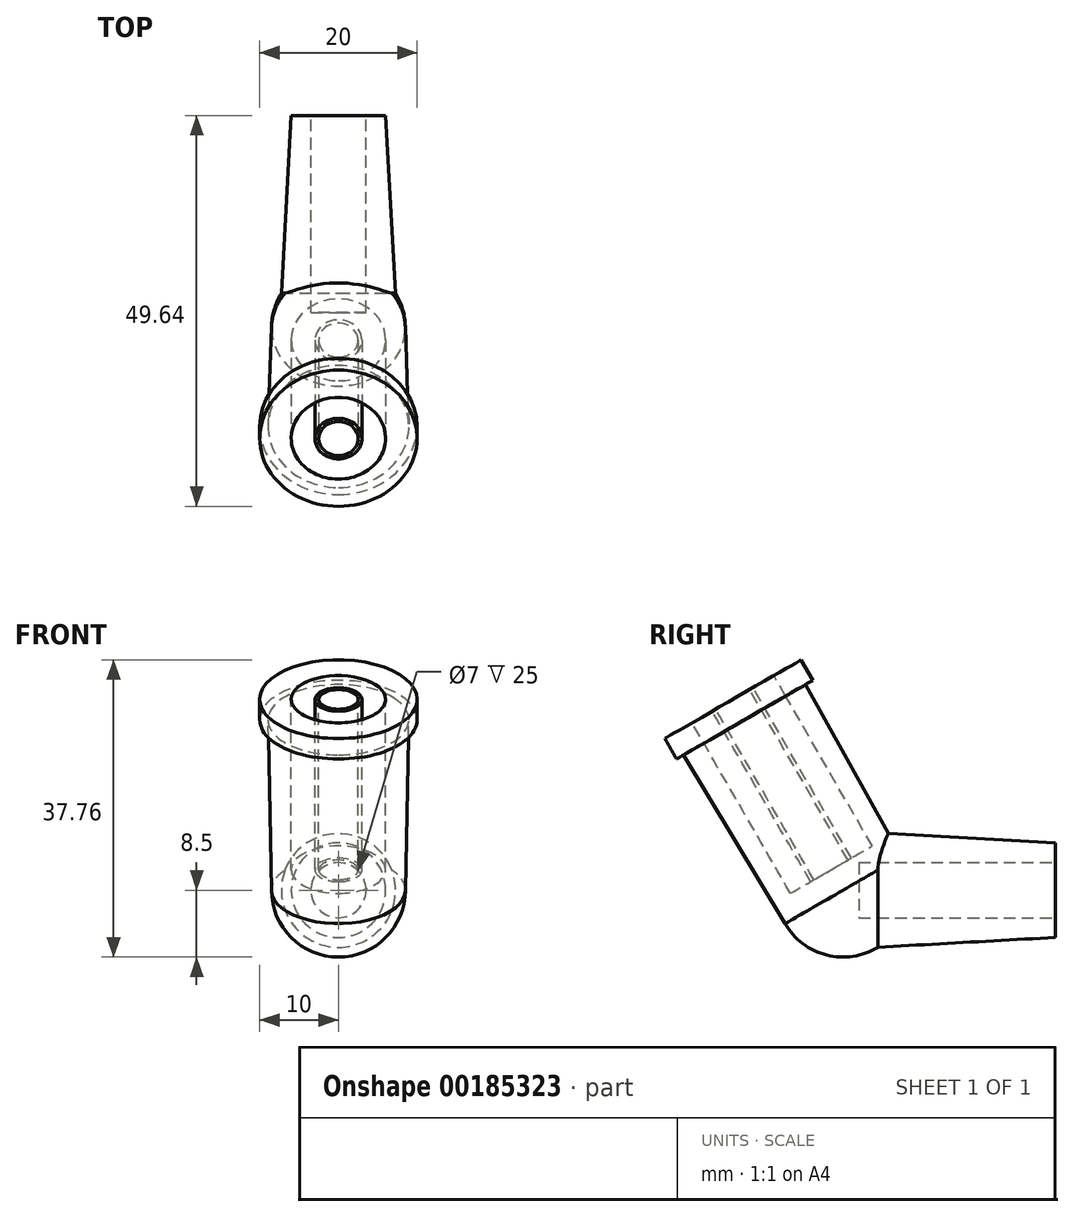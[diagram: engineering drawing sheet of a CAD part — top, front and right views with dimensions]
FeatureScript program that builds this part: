
annotation { "Feature Type Name" : "Feature", "Feature Type Description" : "" }
export const myFeature = defineFeature(function(context is Context, id is Id, definition is map)
    precondition{}
    {
        {
            var Q0;
            Q0=qCreatedBy(makeId("Front.planeOp"),FACE);
            var sketch = newSketch(context, id + "F0", { "sketchPlane" : qUnion([Q0])});
            skCircle(sketch, "E0", {"center": v(0, 0) * mm, "radius": 6 * mm});
            skSolve(sketch);
        }
        {
            var Q0;
            Q0=qCreatedBy(makeId("Front.planeOp"),FACE);
            cPlane(context, id + "F1", {"entities" : qUnion([Q0]), "cplaneType" : CPlaneType.OFFSET, "offset" : 27 * mm, "width" : 150 * mm, "height" : 150 * mm});
        }
        {
            var Q0;
            Q0=qCreatedBy(id+"F1.planeOp",FACE);
            var sketch = newSketch(context, id + "F2", { "sketchPlane" : qUnion([Q0])});
            skCircle(sketch, "E1", {"center": v(0, 0) * mm, "radius": 7.5 * mm});
            skSolve(sketch);
        }
        {
            var Q0;
            Q0=makeQuery(id+"F0.imprint","IMPRINT",FACE,{"disambiguationData":[TD([[makeQuery(id+"F0.imprint","IMPRINT",EDGE,{"derivedFrom":sQuery(id+"F0.wireOp",EDGE,"E0")}),1.0]])]});
            var Q1;
            Q1=makeQuery(id+"F2.imprint","IMPRINT",FACE,{"disambiguationData":[TD([[makeQuery(id+"F2.imprint","IMPRINT",EDGE,{"derivedFrom":sQuery(id+"F2.wireOp",EDGE,"E1")}),1.0]])]});
            loft(context, id + "F3", {"sheetProfilesArray" : [{ "sheetProfileEntities" : qUnion([Q0]) }, { "sheetProfileEntities" : qUnion([Q1]) }]});
        }
        {
            var Q0;
            Q0=qCreatedBy(makeId("Top.planeOp"),FACE);
            cPlane(context, id + "F4", {"entities" : qUnion([Q0]), "cplaneType" : CPlaneType.OFFSET, "offset" : 24.25 * mm, "width" : 150 * mm, "height" : 150 * mm});
        }
        {
            var Q0;
            Q0=qCreatedBy(id+"F4.planeOp",FACE);
            var sketch = newSketch(context, id + "F5", { "sketchPlane" : qUnion([Q0])});
            skLineSegment(sketch, "E2", {"start": v(0, 0) * mm, "end": v(0, -41) * mm});
            skCircle(sketch, "E3", {"center": v(0, -41) * mm, "radius": 9 * mm});
            skLineSegment(sketch, "E4", {"start": v(-9, -41) * mm, "end": v(9, -41) * mm});
            skSolve(sketch);
        }
        {
            var Q0;
            Q0=sQuery(id+"F5.wireOp",EDGE,"E4");
            cPlane(context, id + "F6", {"entities" : qUnion([Q0]), "cplaneType" : CPlaneType.LINE_ANGLE, "offset" : 25 * mm, "angle" : 120 * degree, "width" : 150 * mm, "height" : 150 * mm});
        }
        {
            var Q0;
            Q0=qCreatedBy(id+"F6.planeOp",FACE);
            var sketch = newSketch(context, id + "F7", { "sketchPlane" : qUnion([Q0])});
            skCircle(sketch, "E5", {"center": v(0, -23.38) * mm, "radius": 9 * mm});
            skSolve(sketch);
        }
        {
            var Q0;
            Q0=makeQuery(id+"F3.opLoft","CAP_FACE",FACE,{"disambiguationData":[OSD([makeQuery(id+"F2.imprint","IMPRINT",FACE,{"disambiguationData":[TD([[makeQuery(id+"F2.imprint","IMPRINT",EDGE,{"derivedFrom":sQuery(id+"F2.wireOp",EDGE,"E1")}),1.0]])]})])],"isStart":true});
            var sketch = newSketch(context, id + "F8", { "sketchPlane" : qUnion([Q0])});
            skCircle(sketch, "E6", {"center": v(0, 0) * mm, "radius": 8.5 * mm});
            skLineSegment(sketch, "E7", {"start": v(-8.5, 0) * mm, "end": v(8.5, 0) * mm});
            skSolve(sketch);
        }
        {
            var Q0;
            Q0=qCreatedBy(id+"F6.planeOp",FACE);
            cPlane(context, id + "F9", {"entities" : qUnion([Q0]), "cplaneType" : CPlaneType.OFFSET, "offset" : 28 * mm, "oppositeDirection" : true, "width" : 150 * mm, "height" : 150 * mm});
        }
        {
            var Q0;
            Q0=qCreatedBy(id+"F9.planeOp",FACE);
            var sketch = newSketch(context, id + "F10", { "sketchPlane" : qUnion([Q0])});
            skCircle(sketch, "E8", {"center": v(0, -23.38) * mm, "radius": 8.5 * mm});
            skSolve(sketch);
        }
        {
            var Q1;
            Q1=makeQuery(id+"F7.imprint","IMPRINT",FACE,{"disambiguationData":[TD([[makeQuery(id+"F7.imprint","IMPRINT",EDGE,{"derivedFrom":sQuery(id+"F7.wireOp",EDGE,"E5")}),1.0]])]});
            var Q2;
            Q2=makeQuery(id+"F10.imprint","IMPRINT",FACE,{"disambiguationData":[TD([[makeQuery(id+"F10.imprint","IMPRINT",EDGE,{"derivedFrom":sQuery(id+"F10.wireOp",EDGE,"E8")}),1.0]])]});
            loft(context, id + "F11", {"operationType" : NewBodyOperationType.ADD, "sheetProfilesArray" : [{ "sheetProfileEntities" : qUnion([Q1]) }, { "sheetProfileEntities" : qUnion([Q2]) }]});
        }
        {
            var Q0;
            {var subQ0=sQuery(id+"F8.wireOp",EDGE,"E7");var subQ1=makeQuery(id+"F3.opLoft","MID_CAP_EDGE",EDGE,{"disambiguationData":[OSD([sQuery(id+"F0.wireOp",EDGE,"E0"),sQuery(id+"F2.wireOp",EDGE,"E1")])],"capPos":1.0});var subQ2=makeQuery(id+"F8.imprint","INTERSECT",VERTEX,{"disambiguationData":[OD(0.0)],"derivedFrom":[subQ1,subQ0]});Q0=makeQuery(id+"F8.imprint","IMPRINT",FACE,{"disambiguationData":[TD([[makeQuery(id+"F8.imprint","IMPRINT",EDGE,{"disambiguationData":[TD([[subQ2,-1.0]])],"derivedFrom":subQ0}),-1.0]])]});}
            var Q1;
            {var subQ0=sQuery(id+"F8.wireOp",EDGE,"E7");var subQ1=sQuery(id+"F8.wireOp",EDGE,"E6");var subQ2=makeQuery(id+"F8.imprint","INTERSECT",VERTEX,{"disambiguationData":[OD(0.0)],"derivedFrom":[subQ1,subQ0]});Q1=makeQuery(id+"F8.imprint","IMPRINT",FACE,{"disambiguationData":[TD([[makeQuery(id+"F8.imprint","IMPRINT",EDGE,{"disambiguationData":[TD([[subQ2,-1.0]])],"derivedFrom":subQ1}),1.0]])]});}
            var Q2;
            Q2=sQuery(id+"F8.wireOp",EDGE,"E7");
            revolve(context, id + "F12", {"operationType" : NewBodyOperationType.ADD, "entities" : qUnion([Q0, Q1]), "axis" : qUnion([Q2]), "revolveType" : RevolveType.FULL});
        }
        {
            var Q0;
            Q0=makeQuery(id+"F7.imprint","IMPRINT",FACE,{"disambiguationData":[TD([[makeQuery(id+"F7.imprint","IMPRINT",EDGE,{"derivedFrom":sQuery(id+"F7.wireOp",EDGE,"E5")}),1.0]])]});
            var sketch = newSketch(context, id + "F13", { "sketchPlane" : qUnion([Q0])});
            skCircle(sketch, "E9", {"center": v(0, -23.36) * mm, "radius": 10 * mm});
            skSolve(sketch);
        }
        {
            var Q0;
            Q0 = qSketchRegion(id + "F13", true);
            extrude(context, id + "F14", {"entities" : qUnion([Q0]), "operationType" : NewBodyOperationType.ADD, "oppositeDirection" : true, "depth" : 3 * mm});
        }
        {
            var Q0;
            Q0=makeQuery(id+"F3.opLoft","CAP_FACE",FACE,{"disambiguationData":[OSD([makeQuery(id+"F0.imprint","IMPRINT",FACE,{"disambiguationData":[TD([[makeQuery(id+"F0.imprint","IMPRINT",EDGE,{"derivedFrom":sQuery(id+"F0.wireOp",EDGE,"E0")}),1.0]])]})])],"isStart":true});
            var sketch = newSketch(context, id + "F15", { "sketchPlane" : qUnion([Q0])});
            skCircle(sketch, "E10", {"center": v(0, 0) * mm, "radius": 3.5 * mm});
            skSolve(sketch);
        }
        {
            var Q0;
            Q0 = qSketchRegion(id + "F15", true);
            extrude(context, id + "F16", {"entities" : qUnion([Q0]), "operationType" : NewBodyOperationType.REMOVE, "oppositeDirection" : true, "depth" : 25 * mm});
        }
        {
            var Q0;
            Q0=makeQuery(id+"F7.imprint","IMPRINT",FACE,{"disambiguationData":[TD([[makeQuery(id+"F7.imprint","IMPRINT",EDGE,{"derivedFrom":sQuery(id+"F7.wireOp",EDGE,"E5")}),1.0]])]});
            var sketch = newSketch(context, id + "F17", { "sketchPlane" : qUnion([Q0])});
            skCircle(sketch, "E11", {"center": v(0, -23.37) * mm, "radius": 6 * mm});
            skSolve(sketch);
        }
        {
            var Q0;
            Q0 = qSketchRegion(id + "F17", true);
            extrude(context, id + "F18", {"entities" : qUnion([Q0]), "operationType" : NewBodyOperationType.REMOVE, "oppositeDirection" : true, "depth" : 25 * mm});
        }
        {
            var Q0;
            Q0=makeQuery(id+"F7.imprint","IMPRINT",FACE,{"disambiguationData":[TD([[makeQuery(id+"F7.imprint","IMPRINT",EDGE,{"derivedFrom":sQuery(id+"F7.wireOp",EDGE,"E5")}),1.0]])]});
            var sketch = newSketch(context, id + "F19", { "sketchPlane" : qUnion([Q0])});
            skCircle(sketch, "E12", {"center": v(0, -23.42) * mm, "radius": 2.98 * mm});
            skCircle(sketch, "E13", {"center": v(0, -23.42) * mm, "radius": 2.5 * mm});
            skSolve(sketch);
        }
        {
            var Q0;
            Q0=makeQuery(id+"F19.imprint","IMPRINT",FACE,{"disambiguationData":[TD([[makeQuery(id+"F19.imprint","IMPRINT",EDGE,{"derivedFrom":sQuery(id+"F19.wireOp",EDGE,"E12")}),1.0]])]});
            extrude(context, id + "F20", {"entities" : qUnion([Q0]), "oppositeDirection" : true, "depth" : 25 * mm});
        }
    });
